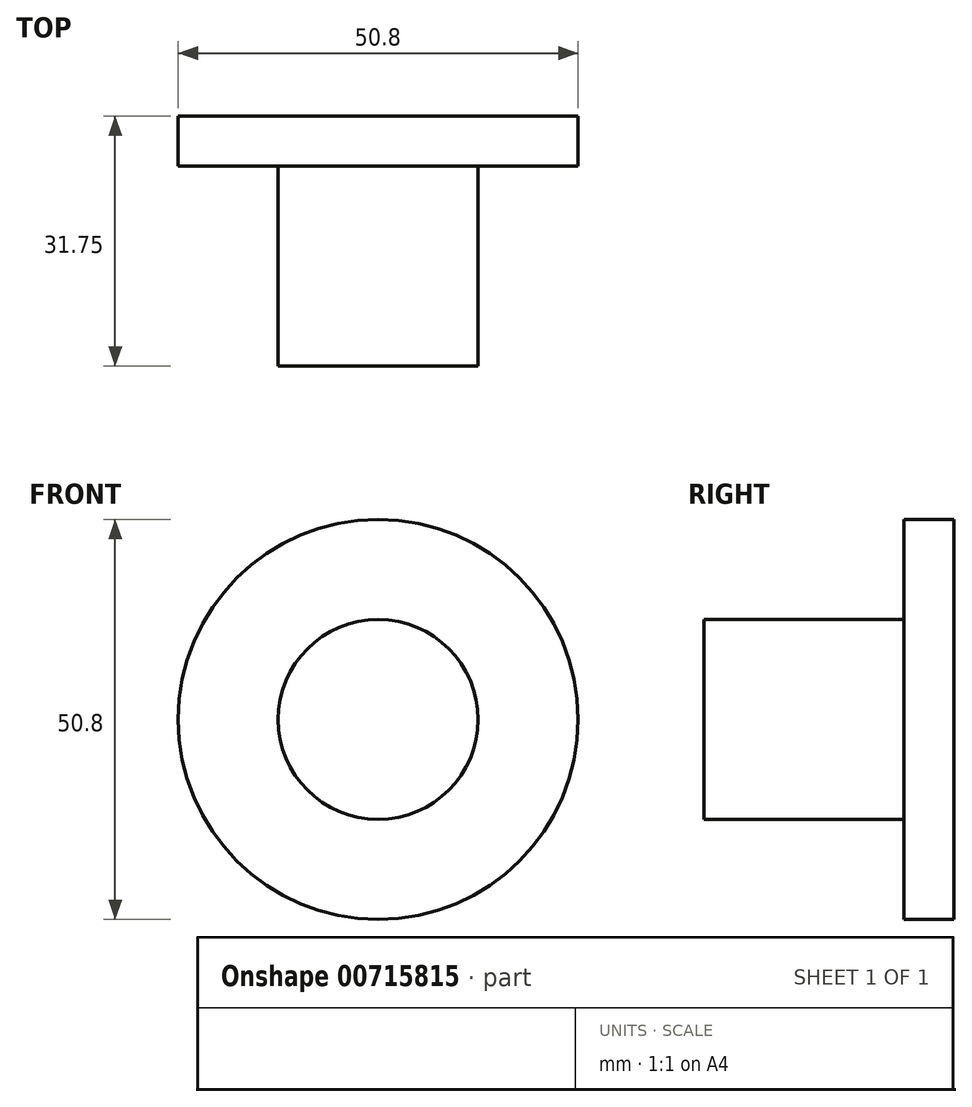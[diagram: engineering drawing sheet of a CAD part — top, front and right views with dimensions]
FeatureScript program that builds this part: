
annotation { "Feature Type Name" : "Feature", "Feature Type Description" : "" }
export const myFeature = defineFeature(function(context is Context, id is Id, definition is map)
    precondition{}
    {
        {
            var Q0;
            Q0=qCreatedBy(makeId("Front.planeOp"),FACE);
            var sketch = newSketch(context, id + "F0", { "sketchPlane" : qUnion([Q0])});
            skCircle(sketch, "E0", {"center": v(0, 0) * mm, "radius": 25.4 * mm});
            skCircle(sketch, "E1", {"center": v(0, 0) * mm, "radius": 12.7 * mm});
            skSolve(sketch);
        }
        {
            var Q0;
            Q0=makeQuery(id+"F0.imprint","IMPRINT",FACE,{"disambiguationData":[TD([[makeQuery(id+"F0.imprint","IMPRINT",EDGE,{"derivedFrom":sQuery(id+"F0.wireOp",EDGE,"E1")}),1.0]])]});
            extrude(context, id + "F1", {"entities" : qUnion([Q0]), "depth" : 31.75 * mm, "offsetDistance" : 25.4 * mm});
        }
        {
            var Q0;
            Q0=makeQuery(id+"F1.opExtrude","CAP_FACE",FACE,{"disambiguationData":[OSD([sQuery(id+"F0.wireOp",EDGE,"E1")])],"isStart":true});
            var sketch = newSketch(context, id + "F2", { "sketchPlane" : qUnion([Q0])});
            skCircle(sketch, "E2", {"center": v(0, 0) * mm, "radius": 25.4 * mm});
            skSolve(sketch);
        }
        {
            var Q0;
            Q0 = qSketchRegion(id + "F2", true);
            extrude(context, id + "F3", {"entities" : qUnion([Q0]), "operationType" : NewBodyOperationType.ADD, "oppositeDirection" : true, "depth" : 6.35 * mm, "offsetDistance" : 25.4 * mm});
        }
    });
